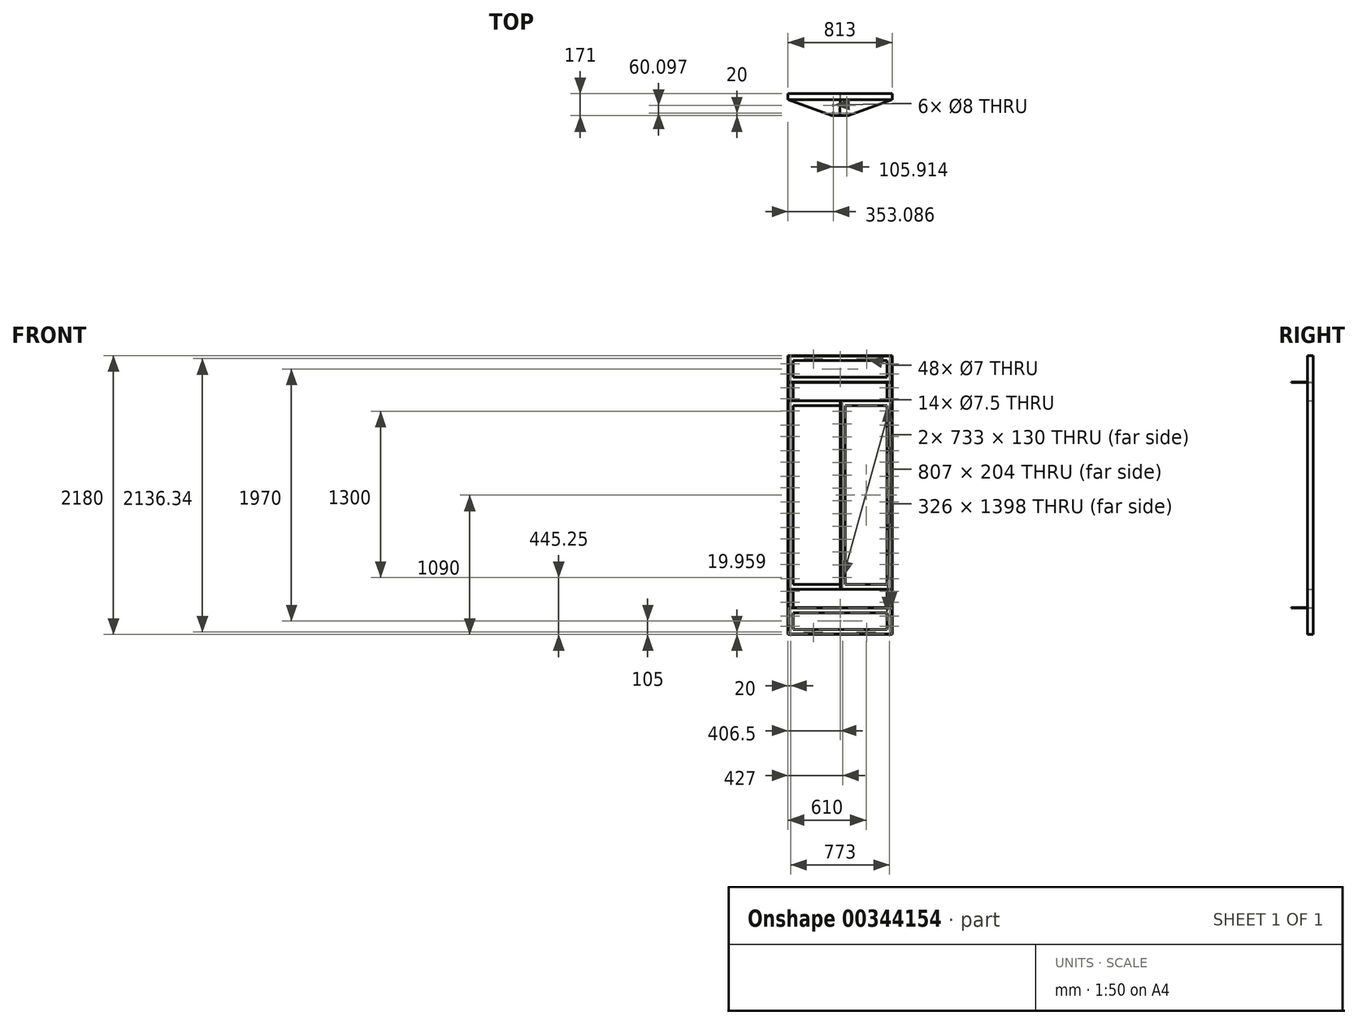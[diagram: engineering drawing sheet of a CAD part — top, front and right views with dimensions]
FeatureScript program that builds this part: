
annotation { "Feature Type Name" : "Feature", "Feature Type Description" : "" }
export const myFeature = defineFeature(function(context is Context, id is Id, definition is map)
    precondition{}
    {
        {
            var Q0;
            Q0=qCreatedBy(makeId("Front.planeOp"),FACE);
            var sketch = newSketch(context, id + "F0", { "sketchPlane" : qUnion([Q0])});
            skLineSegment(sketch, "E0.bottom", {"start": v(-406.5, -1090) * mm, "end": v(406.5, -1090) * mm});
            skLineSegment(sketch, "E0.top", {"start": v(-406.5, 1090) * mm, "end": v(406.5, 1090) * mm});
            skLineSegment(sketch, "E0.left", {"start": v(-406.5, -1090) * mm, "end": v(-406.5, 1090) * mm});
            skLineSegment(sketch, "E0.right", {"start": v(406.5, -1090) * mm, "end": v(406.5, 1090) * mm});
            skPoint(sketch, "E0.middle", {"position": v(0, 0) * mm});
            skLineSegment(sketch, "E1.bottom", {"start": v(-403.5, 1087) * mm, "end": v(403.5, 1087) * mm});
            skLineSegment(sketch, "E1.top", {"start": v(-403.5, -1087) * mm, "end": v(403.5, -1087) * mm});
            skLineSegment(sketch, "E1.left", {"start": v(-403.5, 1087) * mm, "end": v(-403.5, -1087) * mm});
            skLineSegment(sketch, "E1.right", {"start": v(403.5, 1087) * mm, "end": v(403.5, -1087) * mm});
            skLineSegment(sketch, "E2", {"start": v(403.5, 880) * mm, "end": v(-403.5, 880) * mm});
            skLineSegment(sketch, "E3", {"start": v(-403.5, 883) * mm, "end": v(403.5, 883) * mm});
            skLineSegment(sketch, "E4.bottom", {"start": v(-366.5, 1050) * mm, "end": v(366.5, 1050) * mm});
            skLineSegment(sketch, "E4.top", {"start": v(-366.5, 920) * mm, "end": v(366.5, 920) * mm});
            skLineSegment(sketch, "E4.left", {"start": v(-366.5, 1050) * mm, "end": v(-366.5, 920) * mm});
            skLineSegment(sketch, "E4.right", {"start": v(366.5, 1050) * mm, "end": v(366.5, 920) * mm});
            skPoint(sketch, "E4.middle", {"position": v(0, 985) * mm});
            skLineSegment(sketch, "E5", {"start": v(-403.5, -880) * mm, "end": v(403.5, -880) * mm});
            skLineSegment(sketch, "E6", {"start": v(403.5, -883) * mm, "end": v(-403.5, -883) * mm});
            skLineSegment(sketch, "E7.bottom", {"start": v(-366.5, -920) * mm, "end": v(366.5, -920) * mm});
            skLineSegment(sketch, "E7.top", {"start": v(-366.5, -1050) * mm, "end": v(366.5, -1050) * mm});
            skLineSegment(sketch, "E7.left", {"start": v(-366.5, -920) * mm, "end": v(-366.5, -1050) * mm});
            skLineSegment(sketch, "E7.right", {"start": v(366.5, -920) * mm, "end": v(366.5, -1050) * mm});
            skPoint(sketch, "E7.middle", {"position": v(0, -985) * mm});
            skLineSegment(sketch, "E8", {"start": v(-366.5, -880) * mm, "end": v(-366.5, -739) * mm});
            skLineSegment(sketch, "E9", {"start": v(366.5, -880) * mm, "end": v(366.5, -739) * mm});
            skLineSegment(sketch, "E10.bottom", {"start": v(-403.5, -739) * mm, "end": v(403.5, -739) * mm});
            skLineSegment(sketch, "E10.top", {"start": v(-403.5, -736) * mm, "end": v(403.5, -736) * mm});
            skLineSegment(sketch, "E10.left", {"start": v(-403.5, -739) * mm, "end": v(-403.5, -736) * mm});
            skLineSegment(sketch, "E10.right", {"start": v(403.5, -739) * mm, "end": v(403.5, -736) * mm});
            skLineSegment(sketch, "E11.bottom", {"start": v(-403.5, 739) * mm, "end": v(403.5, 739) * mm});
            skLineSegment(sketch, "E11.top", {"start": v(-403.5, 736) * mm, "end": v(403.5, 736) * mm});
            skLineSegment(sketch, "E11.left", {"start": v(-403.5, 739) * mm, "end": v(-403.5, 736) * mm});
            skLineSegment(sketch, "E11.right", {"start": v(403.5, 739) * mm, "end": v(403.5, 736) * mm});
            skLineSegment(sketch, "E12", {"start": v(366.5, 880) * mm, "end": v(366.5, 739) * mm});
            skLineSegment(sketch, "E13", {"start": v(-366.5, 880) * mm, "end": v(-366.5, 739) * mm});
            skLineSegment(sketch, "E14.left", {"start": v(-366.5, 699) * mm, "end": v(-366.5, -699) * mm});
            skLineSegment(sketch, "E14.right", {"start": v(366.5, 699) * mm, "end": v(366.5, -699) * mm});
            skLineSegment(sketch, "E15.bottom", {"start": v(0.5, 739) * mm, "end": v(3.5, 739) * mm});
            skLineSegment(sketch, "E15.top", {"start": v(0.5, -739) * mm, "end": v(3.5, -739) * mm});
            skLineSegment(sketch, "E15.left", {"start": v(0.5, 739) * mm, "end": v(0.5, -739) * mm});
            skLineSegment(sketch, "E15.right", {"start": v(3.5, 739) * mm, "end": v(3.5, -739) * mm});
            skLineSegment(sketch, "E16", {"start": v(40.5, 699) * mm, "end": v(40.5, -699) * mm});
            skLineSegment(sketch, "E17", {"start": v(40.5, -699) * mm, "end": v(366.5, -699) * mm});
            skLineSegment(sketch, "E18", {"start": v(-366.5, 699) * mm, "end": v(0.5, 699) * mm});
            skLineSegment(sketch, "E19", {"start": v(40.5, 699) * mm, "end": v(366.5, 699) * mm});
            skLineSegment(sketch, "E20", {"start": v(-366.5, -699) * mm, "end": v(0.5, -699) * mm});
            skCircle(sketch, "E21", {"center": v(206.5, 1066.3) * mm, "radius": 3.5 * mm});
            skCircle(sketch, "E22", {"center": v(386.5, 1025) * mm, "radius": 3.5 * mm});
            skCircle(sketch, "E23", {"center": v(386.5, 945) * mm, "radius": 3.5 * mm});
            skCircle(sketch, "E24", {"center": v(386.5, 838) * mm, "radius": 3.5 * mm});
            skCircle(sketch, "E25", {"center": v(386.5, 753) * mm, "radius": 3.5 * mm});
            skCircle(sketch, "E26", {"center": v(386.5, 657) * mm, "radius": 3.5 * mm});
            skCircle(sketch, "E27", {"center": v(386.5, 547) * mm, "radius": 3.5 * mm});
            skCircle(sketch, "E28", {"center": v(386.5, 457) * mm, "radius": 3.5 * mm});
            skCircle(sketch, "E29", {"center": v(386.5, 347) * mm, "radius": 3.5 * mm});
            skCircle(sketch, "E30", {"center": v(386.5, 257) * mm, "radius": 3.5 * mm});
            skCircle(sketch, "E31", {"center": v(386.5, 147) * mm, "radius": 3.5 * mm});
            skCircle(sketch, "E32", {"center": v(386.5, 57) * mm, "radius": 3.5 * mm});
            skCircle(sketch, "E33", {"center": v(386.5, -53) * mm, "radius": 3.5 * mm});
            skCircle(sketch, "E34", {"center": v(386.5, -143) * mm, "radius": 3.5 * mm});
            skCircle(sketch, "E35", {"center": v(386.5, -253) * mm, "radius": 3.5 * mm});
            skCircle(sketch, "E36", {"center": v(386.5, -343) * mm, "radius": 3.5 * mm});
            skCircle(sketch, "E37", {"center": v(386.5, -453) * mm, "radius": 3.5 * mm});
            skCircle(sketch, "E38", {"center": v(386.5, -543) * mm, "radius": 3.5 * mm});
            skCircle(sketch, "E39", {"center": v(386.5, -653) * mm, "radius": 3.5 * mm});
            skCircle(sketch, "E40", {"center": v(206.5, -1070.04) * mm, "radius": 3.5 * mm});
            skCircle(sketch, "E41", {"center": v(386.5, -1025) * mm, "radius": 3.5 * mm});
            skCircle(sketch, "E42", {"center": v(386.5, -945) * mm, "radius": 3.5 * mm});
            skCircle(sketch, "E43", {"center": v(386.5, -838) * mm, "radius": 3.5 * mm});
            skCircle(sketch, "E44", {"center": v(386.5, -753) * mm, "radius": 3.5 * mm});
            skLineSegment(sketch, "E45", {"start": v(0, 0) * mm, "end": v(0, 3.63) * mm});
            skCircle(sketch, "E46.MirrorC", {"center": v(-206.5, 1066.3) * mm, "radius": 3.5 * mm});
            skCircle(sketch, "E47.MirrorC", {"center": v(-386.5, 945) * mm, "radius": 3.5 * mm});
            skCircle(sketch, "E48.MirrorC", {"center": v(-386.5, 1025) * mm, "radius": 3.5 * mm});
            skCircle(sketch, "E49.MirrorC", {"center": v(-386.5, 838) * mm, "radius": 3.5 * mm});
            skCircle(sketch, "E50.MirrorC", {"center": v(-386.5, 753) * mm, "radius": 3.5 * mm});
            skCircle(sketch, "E51.MirrorC", {"center": v(-386.5, 457) * mm, "radius": 3.5 * mm});
            skCircle(sketch, "E52.MirrorC", {"center": v(-386.5, 347) * mm, "radius": 3.5 * mm});
            skCircle(sketch, "E53.MirrorC", {"center": v(-386.5, -53) * mm, "radius": 3.5 * mm});
            skCircle(sketch, "E54.MirrorC", {"center": v(-386.5, 257) * mm, "radius": 3.5 * mm});
            skCircle(sketch, "E55.MirrorC", {"center": v(-386.5, 657) * mm, "radius": 3.5 * mm});
            skCircle(sketch, "E56.MirrorC", {"center": v(-386.5, 147) * mm, "radius": 3.5 * mm});
            skCircle(sketch, "E57.MirrorC", {"center": v(-386.5, 547) * mm, "radius": 3.5 * mm});
            skCircle(sketch, "E58.MirrorC", {"center": v(-386.5, 57) * mm, "radius": 3.5 * mm});
            skCircle(sketch, "E59.MirrorC", {"center": v(-386.5, -543) * mm, "radius": 3.5 * mm});
            skCircle(sketch, "E60.MirrorC", {"center": v(-386.5, -143) * mm, "radius": 3.5 * mm});
            skCircle(sketch, "E61.MirrorC", {"center": v(-386.5, -343) * mm, "radius": 3.5 * mm});
            skCircle(sketch, "E62.MirrorC", {"center": v(-386.5, -253) * mm, "radius": 3.5 * mm});
            skCircle(sketch, "E63.MirrorC", {"center": v(-386.5, -653) * mm, "radius": 3.5 * mm});
            skCircle(sketch, "E64.MirrorC", {"center": v(-386.5, -453) * mm, "radius": 3.5 * mm});
            skCircle(sketch, "E65.MirrorC", {"center": v(-386.5, -753) * mm, "radius": 3.5 * mm});
            skCircle(sketch, "E66.MirrorC", {"center": v(-386.5, -838) * mm, "radius": 3.5 * mm});
            skCircle(sketch, "E67.MirrorC", {"center": v(-386.5, -1025) * mm, "radius": 3.5 * mm});
            skCircle(sketch, "E68.MirrorC", {"center": v(-206.5, -1070.04) * mm, "radius": 3.5 * mm});
            skCircle(sketch, "E69.MirrorC", {"center": v(-386.5, -945) * mm, "radius": 3.5 * mm});
            skCircle(sketch, "E70", {"center": v(20.5, 655.25) * mm, "radius": 3.75 * mm});
            skCircle(sketch, "E71", {"center": v(20.5, 555.25) * mm, "radius": 3.75 * mm});
            skCircle(sketch, "E72", {"center": v(20.5, 455.25) * mm, "radius": 3.75 * mm});
            skCircle(sketch, "E73", {"center": v(20.5, 355.25) * mm, "radius": 3.75 * mm});
            skCircle(sketch, "E74", {"center": v(20.5, 255.25) * mm, "radius": 3.75 * mm});
            skCircle(sketch, "E75", {"center": v(20.5, 155.25) * mm, "radius": 3.75 * mm});
            skCircle(sketch, "E76", {"center": v(20.5, 55.25) * mm, "radius": 3.75 * mm});
            skCircle(sketch, "E77", {"center": v(20.5, -44.75) * mm, "radius": 3.75 * mm});
            skCircle(sketch, "E78", {"center": v(20.5, -144.75) * mm, "radius": 3.75 * mm});
            skCircle(sketch, "E79", {"center": v(20.5, -244.75) * mm, "radius": 3.75 * mm});
            skCircle(sketch, "E80", {"center": v(20.5, -344.75) * mm, "radius": 3.75 * mm});
            skCircle(sketch, "E81", {"center": v(20.5, -444.75) * mm, "radius": 3.75 * mm});
            skCircle(sketch, "E82", {"center": v(20.5, -544.75) * mm, "radius": 3.75 * mm});
            skCircle(sketch, "E83", {"center": v(20.5, -644.75) * mm, "radius": 3.75 * mm});
            skSolve(sketch);
        }
        {
            var Q0;
            Q0=makeQuery(id+"F0.imprint","IMPRINT",FACE,{"disambiguationData":[TD([[makeQuery(id+"F0.imprint","IMPRINT",EDGE,{"derivedFrom":sQuery(id+"F0.wireOp",EDGE,"E14.right")}),1.0]])]});
            var Q1;
            {var subQ5=sQuery(id+"F0.wireOp",EDGE,"E12");Q1=makeQuery(id+"F0.imprint","IMPRINT",FACE,{"disambiguationData":[TD([[makeQuery(id+"F0.imprint","IMPRINT",EDGE,{"derivedFrom":subQ5}),1.0]])]});}
            var Q2;
            {var subQ5=sQuery(id+"F0.wireOp",EDGE,"E13");Q2=makeQuery(id+"F0.imprint","IMPRINT",FACE,{"disambiguationData":[TD([[makeQuery(id+"F0.imprint","IMPRINT",EDGE,{"derivedFrom":subQ5}),-1.0]])]});}
            var Q3;
            {var subQ2=sQuery(id+"F0.wireOp",EDGE,"E1.bottom");Q3=makeQuery(id+"F0.imprint","IMPRINT",FACE,{"disambiguationData":[TD([[makeQuery(id+"F0.imprint","IMPRINT",EDGE,{"derivedFrom":subQ2}),-1.0]])]});}
            var Q4;
            {var subQ2=sQuery(id+"F0.wireOp",EDGE,"E1.top");Q4=makeQuery(id+"F0.imprint","IMPRINT",FACE,{"disambiguationData":[TD([[makeQuery(id+"F0.imprint","IMPRINT",EDGE,{"derivedFrom":subQ2}),1.0]])]});}
            var Q5;
            {var subQ5=sQuery(id+"F0.wireOp",EDGE,"E8");Q5=makeQuery(id+"F0.imprint","IMPRINT",FACE,{"disambiguationData":[TD([[makeQuery(id+"F0.imprint","IMPRINT",EDGE,{"derivedFrom":subQ5}),1.0]])]});}
            var Q6;
            {var subQ5=sQuery(id+"F0.wireOp",EDGE,"E9");Q6=makeQuery(id+"F0.imprint","IMPRINT",FACE,{"disambiguationData":[TD([[makeQuery(id+"F0.imprint","IMPRINT",EDGE,{"derivedFrom":subQ5}),-1.0]])]});}
            var Q7;
            Q7=makeQuery(id+"F0.imprint","IMPRINT",FACE,{"disambiguationData":[TD([[makeQuery(id+"F0.imprint","IMPRINT",EDGE,{"derivedFrom":sQuery(id+"F0.wireOp",EDGE,"E14.left")}),-1.0]])]});
            extrude(context, id + "F1", {"entities" : qUnion([Q0, Q1, Q2, Q3, Q4, Q5, Q6, Q7]), "depth" : 3 * mm});
        }
        {
            var Q0;
            {var subQ5=sQuery(id+"F0.wireOp",EDGE,"E15.bottom");Q0=makeQuery(id+"F0.imprint","IMPRINT",FACE,{"disambiguationData":[TD([[makeQuery(id+"F0.imprint","IMPRINT",EDGE,{"derivedFrom":subQ5}),-1.0]])]});}
            var Q1;
            {var subQ0=sQuery(id+"F0.wireOp",EDGE,"E11.left");Q1=makeQuery(id+"F0.imprint","IMPRINT",FACE,{"disambiguationData":[TD([[makeQuery(id+"F0.imprint","IMPRINT",EDGE,{"derivedFrom":subQ0}),1.0]])]});}
            var Q2;
            {var subQ0=sQuery(id+"F0.wireOp",EDGE,"E11.right");Q2=makeQuery(id+"F0.imprint","IMPRINT",FACE,{"disambiguationData":[TD([[makeQuery(id+"F0.imprint","IMPRINT",EDGE,{"derivedFrom":subQ0}),-1.0]])]});}
            var Q3;
            {var subQ0=sQuery(id+"F0.wireOp",EDGE,"E15.left");var subQ7=sQuery(id+"F0.wireOp",EDGE,"E10.top");var subQ8=makeQuery(id+"F0.imprint","INTERSECT",VERTEX,{"derivedFrom":[subQ7,subQ0]});Q3=makeQuery(id+"F0.imprint","IMPRINT",FACE,{"disambiguationData":[TD([[makeQuery(id+"F0.imprint","IMPRINT",EDGE,{"disambiguationData":[TD([[subQ8,-1.0]])],"derivedFrom":subQ7}),1.0]])]});}
            var Q4;
            Q4=makeQuery(id+"F0.imprint","IMPRINT",FACE,{"disambiguationData":[TD([[makeQuery(id+"F0.imprint","IMPRINT",EDGE,{"derivedFrom":sQuery(id+"F0.wireOp",EDGE,"E0.bottom")}),1.0]])]});
            var Q5;
            {var subQ5=sQuery(id+"F0.wireOp",EDGE,"E3");Q5=makeQuery(id+"F0.imprint","IMPRINT",FACE,{"disambiguationData":[TD([[makeQuery(id+"F0.imprint","IMPRINT",EDGE,{"derivedFrom":subQ5}),-1.0]])]});}
            var Q6;
            {var subQ0=sQuery(id+"F0.wireOp",EDGE,"E10.left");Q6=makeQuery(id+"F0.imprint","IMPRINT",FACE,{"disambiguationData":[TD([[makeQuery(id+"F0.imprint","IMPRINT",EDGE,{"derivedFrom":subQ0}),-1.0]])]});}
            var Q7;
            {var subQ0=sQuery(id+"F0.wireOp",EDGE,"E10.right");Q7=makeQuery(id+"F0.imprint","IMPRINT",FACE,{"disambiguationData":[TD([[makeQuery(id+"F0.imprint","IMPRINT",EDGE,{"derivedFrom":subQ0}),1.0]])]});}
            var Q8;
            {var subQ5=sQuery(id+"F0.wireOp",EDGE,"E15.top");Q8=makeQuery(id+"F0.imprint","IMPRINT",FACE,{"disambiguationData":[TD([[makeQuery(id+"F0.imprint","IMPRINT",EDGE,{"derivedFrom":subQ5}),1.0]])]});}
            var Q9;
            {var subQ5=sQuery(id+"F0.wireOp",EDGE,"E6");Q9=makeQuery(id+"F0.imprint","IMPRINT",FACE,{"disambiguationData":[TD([[makeQuery(id+"F0.imprint","IMPRINT",EDGE,{"derivedFrom":subQ5}),-1.0]])]});}
            extrude(context, id + "F2", {"entities" : qUnion([Q0, Q1, Q2, Q3, Q4, Q5, Q6, Q7, Q8, Q9]), "depth" : 46 * mm});
        }
        {
            var Q0;
            Q0=makeQuery(id+"F2.opExtrude","SWEPT_FACE",FACE,{"disambiguationData":[OSD([sQuery(id+"F0.wireOp",EDGE,"E2")])]});
            var sketch = newSketch(context, id + "F3", { "sketchPlane" : qUnion([Q0])});
            skPoint(sketch, "E84.endSnap0", {"position": v(-0.8, 0) * mm});
            skLineSegment(sketch, "E85", {"start": v(-64.96, 170.88) * mm, "end": v(-403.5, 46) * mm});
            skLineSegment(sketch, "E86.MirrorCS", {"start": v(65.04, 171.12) * mm, "end": v(403.5, 46) * mm});
            skLineSegment(sketch, "E87", {"start": v(-403.5, 46) * mm, "end": v(403.5, 46) * mm});
            skCircle(sketch, "E88", {"center": v(-53.41, 150.9) * mm, "radius": 4 * mm});
            skCircle(sketch, "E89", {"center": v(-53.3, 90.9) * mm, "radius": 4 * mm});
            skCircle(sketch, "E90.MirrorC", {"center": v(52.38, 151.1) * mm, "radius": 4 * mm});
            skCircle(sketch, "E91.MirrorC", {"center": v(52.49, 91.1) * mm, "radius": 4 * mm});
            skLineSegment(sketch, "E92", {"start": v(-403.5, 46) * mm, "end": v(-64.96, 170.88) * mm});
            skLineSegment(sketch, "E93", {"start": v(-64.96, 170.88) * mm, "end": v(65.04, 171.12) * mm});
            skLineSegment(sketch, "E94", {"start": v(403.5, 46) * mm, "end": v(-403.5, 46) * mm});
            skLineSegment(sketch, "E95", {"start": v(0, 46) * mm, "end": v(-0.23, 171) * mm});
            skSolve(sketch);
        }
        {
            var Q0;
            Q0=makeQuery(id+"F3.imprint","IMPRINT",FACE,{"disambiguationData":[TD([[makeQuery(id+"F3.imprint","IMPRINT",EDGE,{"derivedFrom":sQuery(id+"F3.wireOp",EDGE,"E88")}),-1.0]])]});
            var Q1;
            Q1=makeQuery(id+"F3.imprint","IMPRINT",FACE,{"disambiguationData":[TD([[makeQuery(id+"F3.imprint","IMPRINT",EDGE,{"derivedFrom":sQuery(id+"F3.wireOp",EDGE,"E90.MirrorC")}),1.0]])]});
            extrude(context, id + "F4", {"entities" : qUnion([Q0, Q1]), "operationType" : NewBodyOperationType.ADD, "oppositeDirection" : true, "depth" : 3 * mm});
        }
        {
            var Q0;
            Q0=makeQuery(id+"F2.opExtrude","SWEPT_FACE",FACE,{"disambiguationData":[OSD([sQuery(id+"F0.wireOp",EDGE,"E5")])]});
            var sketch = newSketch(context, id + "F5", { "sketchPlane" : qUnion([Q0])});
            skLineSegment(sketch, "E96", {"start": v(403.5, -46) * mm, "end": v(65, -171) * mm});
            skLineSegment(sketch, "E97", {"start": v(65, -171) * mm, "end": v(-65, -171) * mm});
            skLineSegment(sketch, "E98", {"start": v(-65, -171) * mm, "end": v(-403.5, -46) * mm});
            skLineSegment(sketch, "E99", {"start": v(-403.5, -46) * mm, "end": v(403.5, -46) * mm});
            skCircle(sketch, "E100", {"center": v(52.5, -151) * mm, "radius": 4 * mm});
            skCircle(sketch, "E101", {"center": v(52.5, -91) * mm, "radius": 4 * mm});
            skLineSegment(sketch, "E102", {"start": v(0, -171) * mm, "end": v(0, -46) * mm});
            skCircle(sketch, "E103.MirrorC", {"center": v(-52.5, -151) * mm, "radius": 4 * mm});
            skCircle(sketch, "E104.MirrorC", {"center": v(-52.5, -91) * mm, "radius": 4 * mm});
            skSolve(sketch);
        }
        {
            var Q0;
            {var subQ1=sQuery(id+"F5.wireOp",EDGE,"E98");Q0=makeQuery(id+"F5.imprint","IMPRINT",FACE,{"disambiguationData":[TD([[makeQuery(id+"F5.imprint","IMPRINT",EDGE,{"derivedFrom":subQ1}),-1.0]])]});}
            var Q1;
            {var subQ1=sQuery(id+"F5.wireOp",EDGE,"E96");Q1=makeQuery(id+"F5.imprint","IMPRINT",FACE,{"disambiguationData":[TD([[makeQuery(id+"F5.imprint","IMPRINT",EDGE,{"derivedFrom":subQ1}),-1.0]])]});}
            extrude(context, id + "F6", {"entities" : qUnion([Q0, Q1]), "oppositeDirection" : true, "depth" : 3 * mm});
        }
        {
            var Q0;
            {var subQ0=sQuery(id+"F0.wireOp",EDGE,"E11.top");Q0=makeQuery(id+"F2.opExtrude","SWEPT_FACE",FACE,{"disambiguationData":[OSD([subQ0]),TDD([makeQuery(id+"F0.imprint","IMPRINT",EDGE,{"disambiguationData":[TD([[makeQuery(id+"F0.imprint","INTERSECT",VERTEX,{"derivedFrom":[subQ0,sQuery(id+"F0.wireOp",EDGE,"E15.left")]}),1.0]])],"derivedFrom":subQ0})])]});}
            var sketch = newSketch(context, id + "F7", { "sketchPlane" : qUnion([Q0])});
            skCircle(sketch, "E105", {"center": v(-52.5, 31) * mm, "radius": 3.25 * mm});
            skSolve(sketch);
        }
        {
            var Q0;
            Q0=makeQuery(id+"F7.imprint","IMPRINT",FACE,{"disambiguationData":[TD([[makeQuery(id+"F7.imprint","IMPRINT",EDGE,{"derivedFrom":sQuery(id+"F7.wireOp",EDGE,"E105")}),1.0]])]});
            extrude(context, id + "F8", {"entities" : qUnion([Q0]), "operationType" : NewBodyOperationType.REMOVE, "oppositeDirection" : true, "depth" : 4 * mm});
        }
        {
            var Q0;
            {var subQ0=sQuery(id+"F0.wireOp",EDGE,"E11.top");Q0=makeQuery(id+"F2.opExtrude","SWEPT_FACE",FACE,{"disambiguationData":[OSD([subQ0]),TDD([makeQuery(id+"F0.imprint","IMPRINT",EDGE,{"disambiguationData":[TD([[makeQuery(id+"F0.imprint","INTERSECT",VERTEX,{"derivedFrom":[subQ0,sQuery(id+"F0.wireOp",EDGE,"E15.right")]}),-1.0]])],"derivedFrom":subQ0})])]});}
            var sketch = newSketch(context, id + "F9", { "sketchPlane" : qUnion([Q0])});
            skCircle(sketch, "E106", {"center": v(52.5, 31) * mm, "radius": 3.25 * mm});
            skSolve(sketch);
        }
        {
            var Q0;
            Q0=makeQuery(id+"F9.imprint","IMPRINT",FACE,{"disambiguationData":[TD([[makeQuery(id+"F9.imprint","IMPRINT",EDGE,{"derivedFrom":sQuery(id+"F9.wireOp",EDGE,"E106")}),1.0]])]});
            extrude(context, id + "F10", {"entities" : qUnion([Q0]), "operationType" : NewBodyOperationType.REMOVE, "oppositeDirection" : true, "depth" : 3 * mm});
        }
        {
            var Q0;
            {var subQ0=sQuery(id+"F0.wireOp",EDGE,"E10.top");Q0=makeQuery(id+"F2.opExtrude","SWEPT_FACE",FACE,{"disambiguationData":[OSD([subQ0]),TDD([makeQuery(id+"F0.imprint","IMPRINT",EDGE,{"disambiguationData":[TD([[makeQuery(id+"F0.imprint","INTERSECT",VERTEX,{"derivedFrom":[subQ0,sQuery(id+"F0.wireOp",EDGE,"E15.right")]}),-1.0]])],"derivedFrom":subQ0})])]});}
            var sketch = newSketch(context, id + "F11", { "sketchPlane" : qUnion([Q0])});
            skCircle(sketch, "E107", {"center": v(52.5, -31) * mm, "radius": 3.5 * mm});
            skSolve(sketch);
        }
        {
            var Q0;
            {var subQ0=sQuery(id+"F0.wireOp",EDGE,"E10.top");Q0=makeQuery(id+"F2.opExtrude","SWEPT_FACE",FACE,{"disambiguationData":[OSD([subQ0]),TDD([makeQuery(id+"F0.imprint","IMPRINT",EDGE,{"disambiguationData":[TD([[makeQuery(id+"F0.imprint","INTERSECT",VERTEX,{"derivedFrom":[subQ0,sQuery(id+"F0.wireOp",EDGE,"E15.left")]}),1.0]])],"derivedFrom":subQ0})])]});}
            var sketch = newSketch(context, id + "F12", { "sketchPlane" : qUnion([Q0])});
            skCircle(sketch, "E108", {"center": v(-53.5, -31) * mm, "radius": 3.5 * mm});
            skSolve(sketch);
        }
        {
            var Q0;
            Q0 = qSketchRegion(id + "F12", true);
            extrude(context, id + "F13", {"entities" : qUnion([Q0]), "operationType" : NewBodyOperationType.REMOVE, "oppositeDirection" : true, "depth" : 3 * mm});
        }
        {
            var Q0;
            Q0=makeQuery(id+"F11.imprint","IMPRINT",FACE,{"disambiguationData":[TD([[makeQuery(id+"F11.imprint","IMPRINT",EDGE,{"derivedFrom":sQuery(id+"F11.wireOp",EDGE,"E107")}),1.0]])]});
            extrude(context, id + "F14", {"entities" : qUnion([Q0]), "operationType" : NewBodyOperationType.REMOVE, "oppositeDirection" : true, "depth" : 3 * mm});
        }
    });
